# Revit family: ledhighbay-p4_220w-5700-as-ble_545001025400
name_source: partatom
category: Leuchten
revit_build: Autodesk Revit 2016 (Build: 20190508_0715(x64)
units: mm (PartAtom-declared; Revit-internal decimal feet)

## family parameters
Basisbauteil = Fläche
Beim Laden mit Abzugskörper schneiden = Nein
Bemaßung runder Anschluss = Durchmesser verwenden
Gemeinsam genutzt = Nein
Lichtquelle = Nein
Raumberechnungspunkt = Nein
Teiletyp = Normal

## types (1)
- LEDHighbay-P4 220W-5700-AS-BLE (1 x LED, 30400 lm)
    Approval mark = CE, ENEC
    Beschreibung = NEW: Very high efficacy of 145 lm/W. High quality LED Highbay solution with advanced ultra slim design. Equipped with IP68 connector.
    CIE Flux Codes = 64 90 98 99 100
    Control Gear = Electronic ballast
    Height = 82 mm  [stored 0.269029 ft]
    Hersteller = OPPLE
    Lamp Light Flux = 30400 lm
    Lamp count = 1
    Lampe = 1 x LED
    Length = 408 mm
    Luminous efficacy = 138 lm/W
    ModVariant = Nein
    Modell = 545001025400
    Mounting Place = Ceiling
    Mounting Type = Pendant
    Number of Poles = 1
    OnlyDefault = Ja
    Power Factor = 1
    Product Name = LEDHighbay-P4 220W-5700-AS-BLE
    Product group = Highbay Performer G4
    ProductGroupID = 903
    Protection Class = Protection class I
    Protection Degree = IP 66
    RLX_Detail_Level = 1
    RlxData = <blob elided: 254273 chars, md5=8747a475>
    Scheinlast = 220 VA
    Socket = socket
    Standby Power = 0 W
    System Light Flux = 30400 lm
    System Power = 220 W
    Typenbild = product20highbay20performer20g4.jpg
    Typenkommentare = Product without accessories
    URL = http://relux.com
    VarID = ---
    Voltage = 0 V
    Vorgabe-Ansicht = 1800 mm
    Weight = 0.00 kg
    Width = 0 mm  [stored 0 ft]

note: [stored X ft] marks values corroborated as IEEE doubles in the binary element streams (Revit-internal decimal feet)

## geometry (parser evidence)
native form markers: Blend x4, Sweep x12
no freeform markers — native parametric forms only
